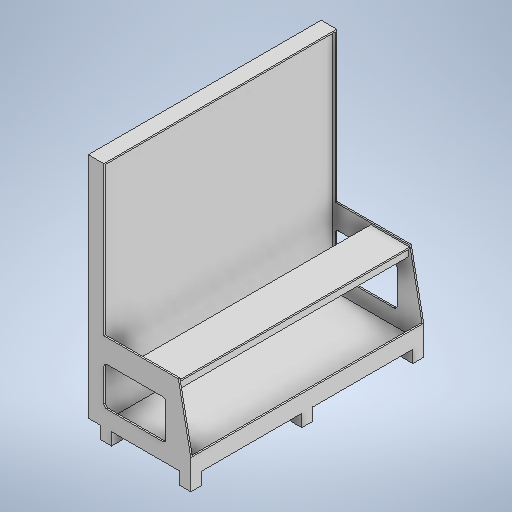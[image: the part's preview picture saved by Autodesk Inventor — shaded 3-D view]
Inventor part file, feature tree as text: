
AUTODESK INVENTOR PART (.ipt)
format: ipt  version: 2025 (Build 290162010, 162A)  size: 361,472 bytes
history: native  units: mm
features: sketch x8, extrude x7
ambient origin geometry x8: Origin, YZ Plane, XZ Plane, XY Plane, X Axis, Y Axis, Z Axis, Center Point
bodies: Solid1 (feature_tree)
feature tree (15):
  extrude  "Extrusion1"  Depth=100.0mm
  extrude  "Extrusion2"  Depth=190.0mm
  extrude  "Extrusion3"  Depth=590.0mm
  extrude  "Extrusion4"  Depth=70.0mm
  extrude  "Extrusion5"  Depth=30.0mm
  extrude  "Extrusion6"  Depth=10.0mm
  extrude  "Extrusion7"  Depth=10.0mm
  sketch  "Sketch1"  dims[d0=1550.0mm d1=100.0mm]
  sketch  "Sketch2"  dims[d4=480.0mm d5=590.0mm]
  sketch  "Sketch Rectangular Pattern1"  dims[d2=660.0mm d3=190.0mm]
  sketch  "Sketch3"  dims[d6=1500.0mm d7=0.0mm d8=70.0mm]
  sketch  "Sketch4"  dims[d9=70.0mm d18=30.0mm d20=715.0mm d21=20.0mm d23=510.0mm]
  sketch  "Sketch5"  dims[d26=80.0mm d27=0.0mm d28=10.0mm]
  sketch  "Sketch6"  dims[d30=10.0mm d31=10.0mm]
  sketch  "Sketch8"  dims[d32=10.0mm d33=70.0mm d34=0.0mm d35=400.0mm d36=250.0mm d37=100.0mm d38=110.0mm d39=20.0mm d40=0.0mm d41=0.0mm d42=10.0mm d43=10.0mm d44=10.0mm d45=580.0mm d46=0.0mm d47=10.0mm d48=100.0mm d49=0.0mm d50=10.0mm d51=250.0mm d52=10.0mm d53=10.0mm d54=10.0mm d55=10.0mm d56=10.0mm d57=50.0mm d58=10.0mm d59=1480.0mm d60=0.0mm]
